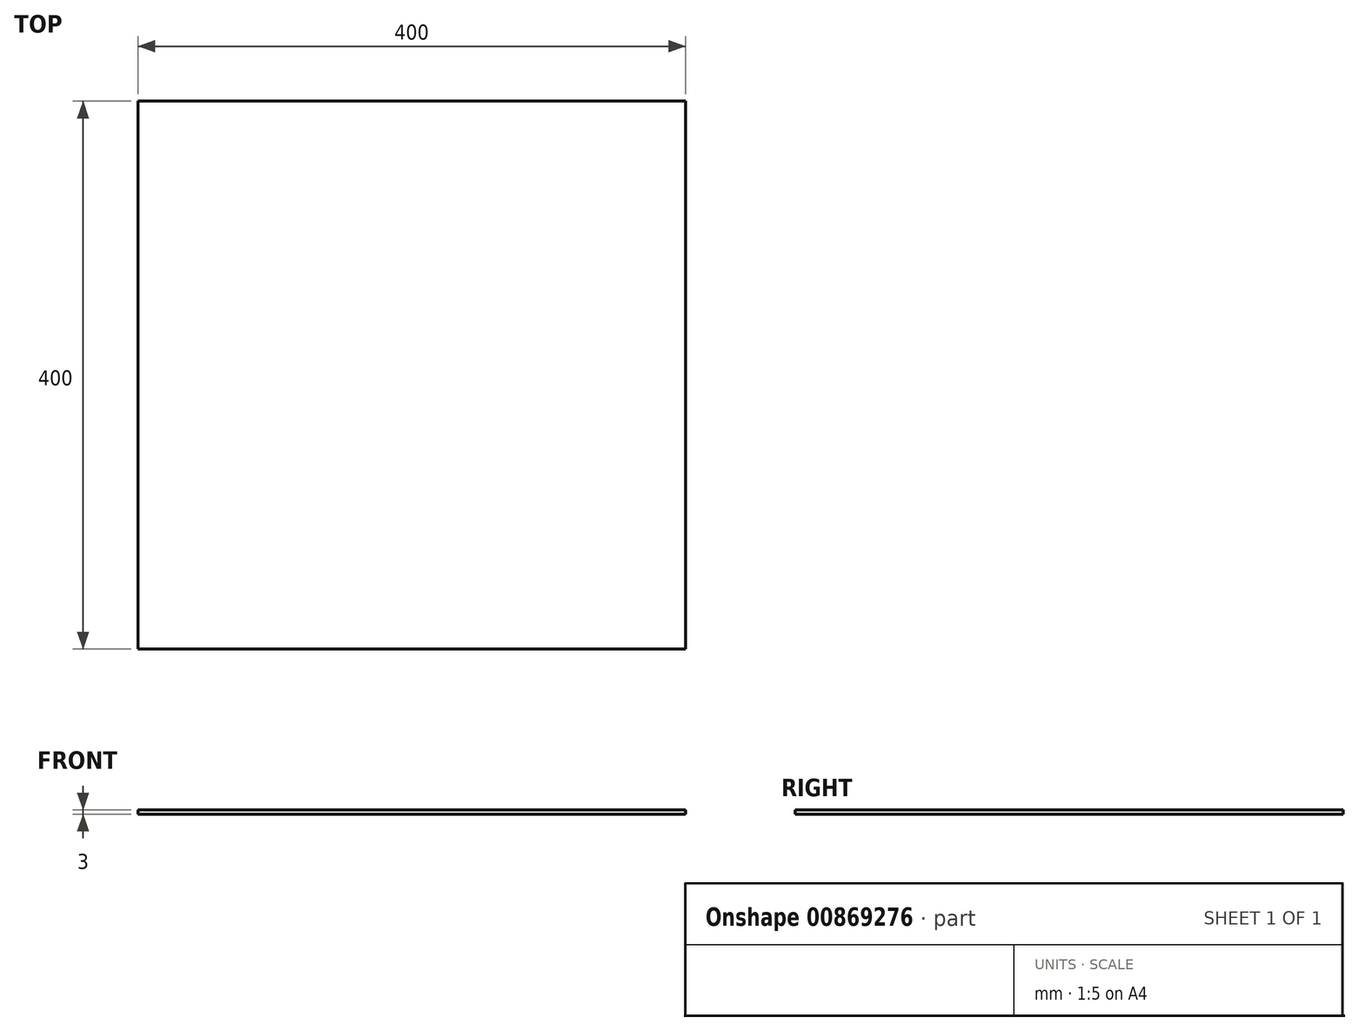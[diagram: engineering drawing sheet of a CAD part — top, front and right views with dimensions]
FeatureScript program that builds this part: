
annotation { "Feature Type Name" : "Feature", "Feature Type Description" : "" }
export const myFeature = defineFeature(function(context is Context, id is Id, definition is map)
    precondition{}
    {
        {
            var Q0;
            Q0=qCreatedBy(makeId("Top.planeOp"),FACE);
            var sketch = newSketch(context, id + "F0", { "sketchPlane" : qUnion([Q0])});
            skLineSegment(sketch, "E0.bottom", {"start": v(200, -200) * mm, "end": v(-200, -200) * mm});
            skLineSegment(sketch, "E0.top", {"start": v(200, 200) * mm, "end": v(-200, 200) * mm});
            skLineSegment(sketch, "E0.left", {"start": v(200, -200) * mm, "end": v(200, 200) * mm});
            skLineSegment(sketch, "E0.right", {"start": v(-200, -200) * mm, "end": v(-200, 200) * mm});
            skPoint(sketch, "E0.middle", {"position": v(0, 0) * mm});
            skSolve(sketch);
        }
        {
            var Q0;
            Q0=makeQuery(id+"F0.imprint","IMPRINT",FACE,{"disambiguationData":[TD([[makeQuery(id+"F0.imprint","IMPRINT",EDGE,{"derivedFrom":sQuery(id+"F0.wireOp",EDGE,"E0.bottom")}),-1.0]])]});
            extrude(context, id + "F1", {"entities" : qUnion([Q0]), "depth" : 3 * mm, "offsetDistance" : 25 * mm});
        }
    });
